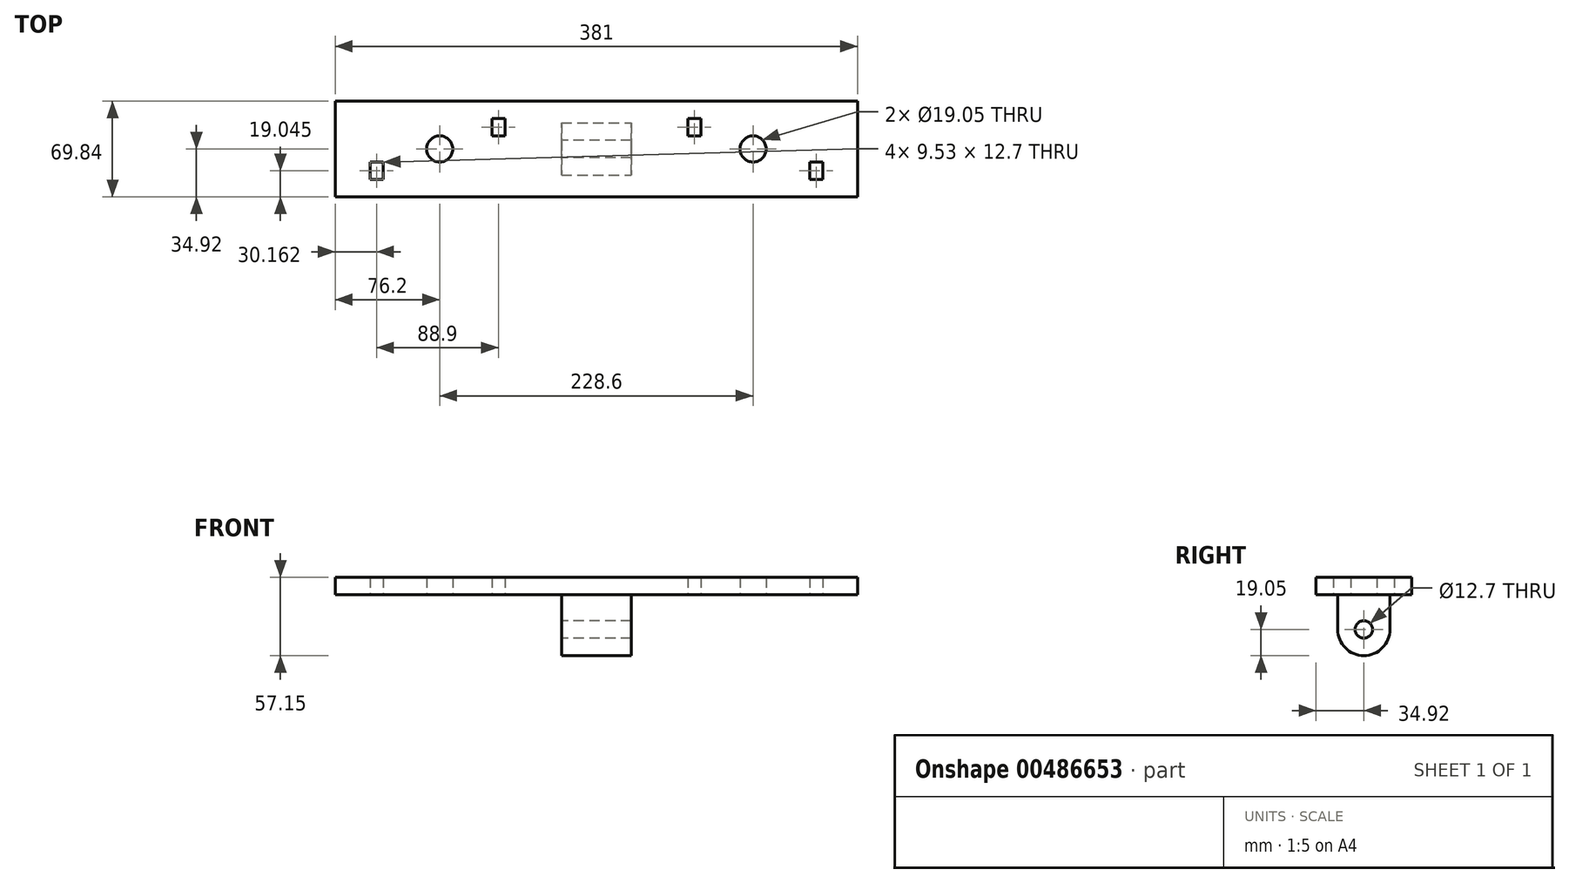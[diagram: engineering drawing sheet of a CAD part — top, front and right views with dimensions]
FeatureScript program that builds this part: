
annotation { "Feature Type Name" : "Feature", "Feature Type Description" : "" }
export const myFeature = defineFeature(function(context is Context, id is Id, definition is map)
    precondition{}
    {
        {
            var Q0;
            Q0=qCreatedBy(makeId("Top.planeOp"),FACE);
            var sketch = newSketch(context, id + "F0", { "sketchPlane" : qUnion([Q0])});
            skLineSegment(sketch, "E0.bottom", {"start": v(-190.5, 34.93) * mm, "end": v(190.5, 34.93) * mm});
            skLineSegment(sketch, "E0.top", {"start": v(-190.5, -34.93) * mm, "end": v(190.5, -34.93) * mm});
            skLineSegment(sketch, "E0.left", {"start": v(-190.5, 34.93) * mm, "end": v(-190.5, -34.93) * mm});
            skLineSegment(sketch, "E0.right", {"start": v(190.5, 34.93) * mm, "end": v(190.5, -34.93) * mm});
            skPoint(sketch, "E0.middle", {"position": v(0, 0) * mm});
            skLineSegment(sketch, "E1.bottom", {"start": v(-165.1, -9.53) * mm, "end": v(-155.58, -9.53) * mm});
            skLineSegment(sketch, "E1.top", {"start": v(-165.1, -22.23) * mm, "end": v(-155.58, -22.23) * mm});
            skLineSegment(sketch, "E1.left", {"start": v(-165.1, -9.53) * mm, "end": v(-165.1, -22.23) * mm});
            skLineSegment(sketch, "E1.right", {"start": v(-155.58, -9.53) * mm, "end": v(-155.58, -22.23) * mm});
            skPoint(sketch, "E1.middle", {"position": v(-160.34, -15.88) * mm});
            skPoint(sketch, "E2.MirrorP", {"position": v(160.34, -15.88) * mm});
            skLineSegment(sketch, "E3.MirrorCS", {"start": v(165.1, -9.53) * mm, "end": v(155.58, -9.53) * mm});
            skLineSegment(sketch, "E4.MirrorCS", {"start": v(165.1, -9.53) * mm, "end": v(165.1, -22.23) * mm});
            skLineSegment(sketch, "E5.MirrorCS", {"start": v(155.58, -9.53) * mm, "end": v(155.58, -22.23) * mm});
            skLineSegment(sketch, "E6.MirrorCS", {"start": v(165.1, -22.23) * mm, "end": v(155.58, -22.23) * mm});
            skCircle(sketch, "E7", {"center": v(-114.3, 0) * mm, "radius": 9.53 * mm});
            skCircle(sketch, "E8.MirrorC", {"center": v(114.3, 0) * mm, "radius": 9.53 * mm});
            skLineSegment(sketch, "E9.bottom", {"start": v(-76.2, 22.22) * mm, "end": v(-66.68, 22.22) * mm});
            skLineSegment(sketch, "E9.top", {"start": v(-76.2, 9.52) * mm, "end": v(-66.68, 9.52) * mm});
            skLineSegment(sketch, "E9.left", {"start": v(-76.2, 22.22) * mm, "end": v(-76.2, 9.52) * mm});
            skLineSegment(sketch, "E9.right", {"start": v(-66.68, 22.22) * mm, "end": v(-66.68, 9.52) * mm});
            skPoint(sketch, "E9.middle", {"position": v(-71.44, 15.87) * mm});
            skLineSegment(sketch, "E10.MirrorCS", {"start": v(66.68, 22.22) * mm, "end": v(66.68, 9.52) * mm});
            skLineSegment(sketch, "E11.MirrorCS", {"start": v(76.2, 9.52) * mm, "end": v(66.68, 9.52) * mm});
            skPoint(sketch, "E12.MirrorP", {"position": v(71.44, 15.87) * mm});
            skLineSegment(sketch, "E13.MirrorCS", {"start": v(76.2, 22.22) * mm, "end": v(66.68, 22.22) * mm});
            skLineSegment(sketch, "E14.MirrorCS", {"start": v(76.2, 22.22) * mm, "end": v(76.2, 9.52) * mm});
            skPoint(sketch, "E15", {"position": v(19.05, 0) * mm});
            skPoint(sketch, "E16.MirrorP", {"position": v(-19.05, 0) * mm});
            skLineSegment(sketch, "E17", {"start": v(-19.05, 0) * mm, "end": v(19.05, 0) * mm});
            skSolve(sketch);
        }
        {
            var Q0;
            Q0=makeQuery(id+"F0.imprint","IMPRINT",FACE,{"disambiguationData":[TD([[makeQuery(id+"F0.imprint","IMPRINT",EDGE,{"derivedFrom":sQuery(id+"F0.wireOp",EDGE,"E0.bottom")}),-1.0]])]});
            extrude(context, id + "F1", {"entities" : qUnion([Q0]), "depth" : 12.7 * mm});
        }
        {
            var Q0;
            Q0=makeQuery(id+"F1.opExtrude","CAP_FACE",FACE,{"disambiguationData":[OSD([sQuery(id+"F0.wireOp",EDGE,"E0.bottom"),sQuery(id+"F0.wireOp",EDGE,"E0.top"),sQuery(id+"F0.wireOp",EDGE,"E0.left"),sQuery(id+"F0.wireOp",EDGE,"E0.right"),sQuery(id+"F0.wireOp",EDGE,"E1.bottom"),sQuery(id+"F0.wireOp",EDGE,"E1.top"),sQuery(id+"F0.wireOp",EDGE,"E1.left"),sQuery(id+"F0.wireOp",EDGE,"E1.right"),sQuery(id+"F0.wireOp",EDGE,"E3.MirrorCS"),sQuery(id+"F0.wireOp",EDGE,"E4.MirrorCS"),sQuery(id+"F0.wireOp",EDGE,"E5.MirrorCS"),sQuery(id+"F0.wireOp",EDGE,"E6.MirrorCS"),sQuery(id+"F0.wireOp",EDGE,"E7"),sQuery(id+"F0.wireOp",EDGE,"E8.MirrorC"),sQuery(id+"F0.wireOp",EDGE,"E9.bottom"),sQuery(id+"F0.wireOp",EDGE,"E9.top"),sQuery(id+"F0.wireOp",EDGE,"E9.left"),sQuery(id+"F0.wireOp",EDGE,"E9.right"),sQuery(id+"F0.wireOp",EDGE,"E10.MirrorCS"),sQuery(id+"F0.wireOp",EDGE,"E11.MirrorCS"),sQuery(id+"F0.wireOp",EDGE,"E13.MirrorCS"),sQuery(id+"F0.wireOp",EDGE,"E14.MirrorCS")])],"isStart":true});
            var sketch = newSketch(context, id + "F2", { "sketchPlane" : qUnion([Q0])});
            skLineSegment(sketch, "E18.bottom", {"start": v(-25.4, 19.05) * mm, "end": v(25.4, 19.05) * mm});
            skLineSegment(sketch, "E18.top", {"start": v(-25.4, -19.05) * mm, "end": v(25.4, -19.05) * mm});
            skLineSegment(sketch, "E18.left", {"start": v(-25.4, 19.05) * mm, "end": v(-25.4, -19.05) * mm});
            skLineSegment(sketch, "E18.right", {"start": v(25.4, 19.05) * mm, "end": v(25.4, -19.05) * mm});
            skPoint(sketch, "E18.middle", {"position": v(0, 0) * mm});
            skSolve(sketch);
        }
        {
            var Q0;
            Q0 = qSketchRegion(id + "F2", true);
            extrude(context, id + "F3", {"entities" : qUnion([Q0]), "operationType" : NewBodyOperationType.ADD, "depth" : 25.4 * mm});
        }
        {
            var Q0;
            Q0=makeQuery(id+"F3.opExtrude","CAP_FACE",FACE,{"disambiguationData":[OSD([sQuery(id+"F2.wireOp",EDGE,"E18.bottom"),sQuery(id+"F2.wireOp",EDGE,"E18.top"),sQuery(id+"F2.wireOp",EDGE,"E18.left"),sQuery(id+"F2.wireOp",EDGE,"E18.right")])],"isStart":false});
            var sketch = newSketch(context, id + "F4", { "sketchPlane" : qUnion([Q0])});
            skLineSegment(sketch, "E19", {"start": v(-25.4, 0) * mm, "end": v(25.4, 0) * mm});
            skSolve(sketch);
        }
        {
            var Q0;
            {var subQ0=sQuery(id+"F4.wireOp",EDGE,"E19");Q0=makeQuery(id+"F4.imprint","IMPRINT",FACE,{"disambiguationData":[TD([[makeQuery(id+"F4.imprint","IMPRINT",EDGE,{"derivedFrom":subQ0}),-1.0]])]});}
            var Q1;
            Q1=sQuery(id+"F4.wireOp",EDGE,"E19");
            revolve(context, id + "F5", {"operationType" : NewBodyOperationType.ADD, "entities" : qUnion([Q0]), "axis" : qUnion([Q1]), "revolveType" : RevolveType.FULL});
        }
        {
            var Q0;
            {var subQ0=sQuery(id+"F2.wireOp",EDGE,"E18.left");Q0=makeQuery(id+"F5.boolean.opBoolean","MERGE",FACE,{"derivedFrom":[makeQuery(id+"F3.opExtrude","SWEPT_FACE",FACE,{"disambiguationData":[OSD([subQ0])]}),makeQuery(id+"F5.opRevolve","SWEPT_FACE",FACE,{"disambiguationData":[OSD([subQ0])]})]});}
            var sketch = newSketch(context, id + "F6", { "sketchPlane" : qUnion([Q0])});
            skCircle(sketch, "E20", {"center": v(0, -25.4) * mm, "radius": 6.35 * mm});
            skSolve(sketch);
        }
        {
            var Q0;
            Q0 = qSketchRegion(id + "F6", true);
            extrude(context, id + "F7", {"entities" : qUnion([Q0]), "operationType" : NewBodyOperationType.REMOVE, "oppositeDirection" : true, "depth" : 76.2 * mm});
        }
    });
